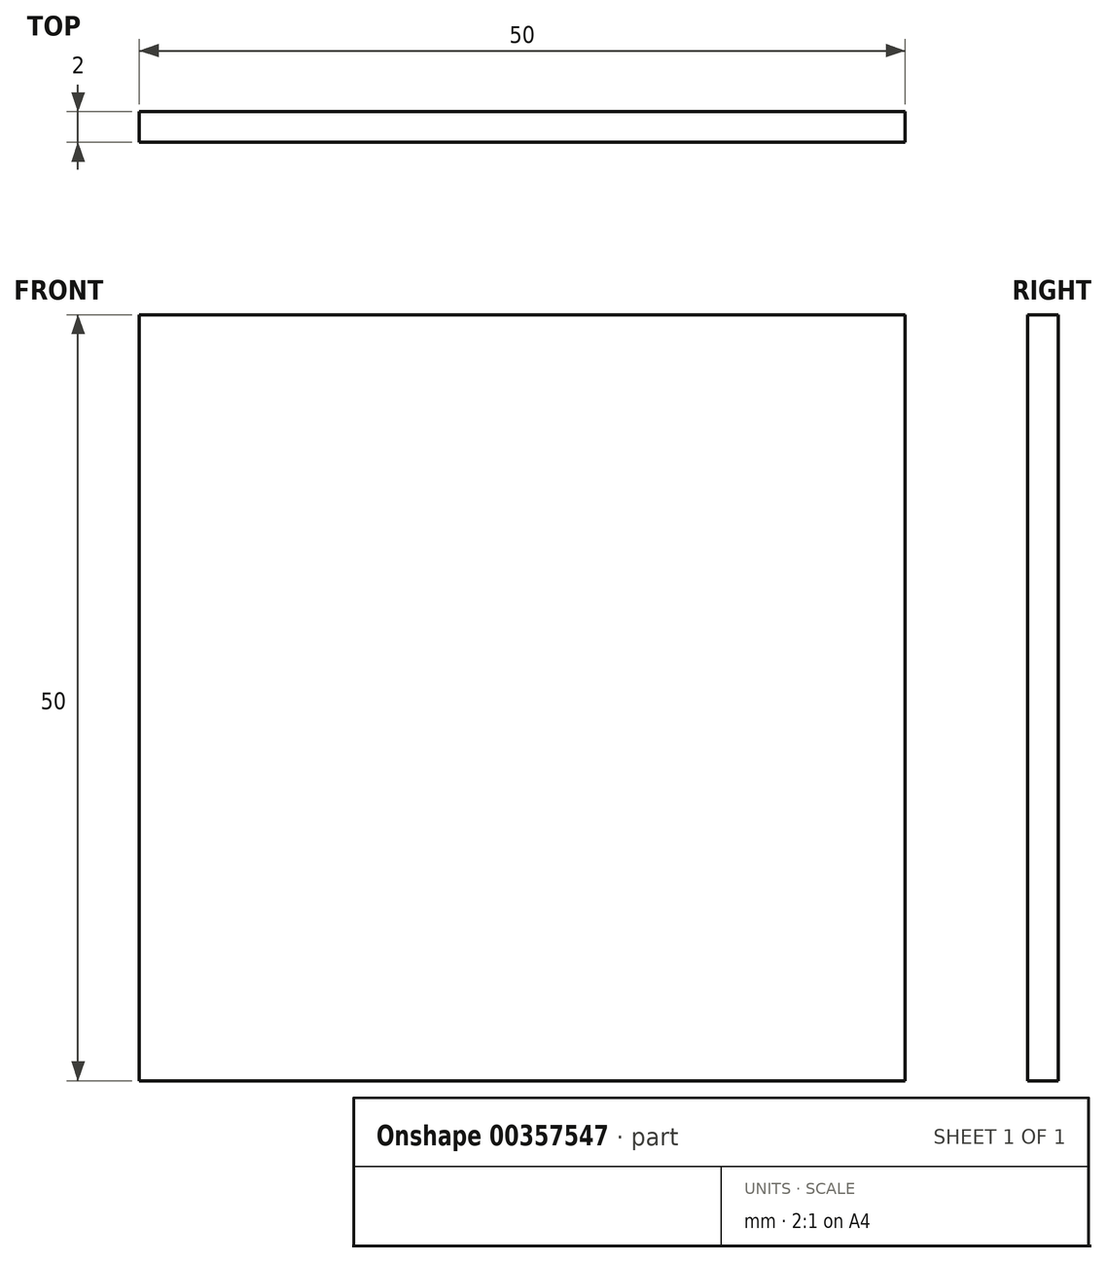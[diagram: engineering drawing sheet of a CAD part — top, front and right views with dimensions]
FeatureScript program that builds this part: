
annotation { "Feature Type Name" : "Feature", "Feature Type Description" : "" }
export const myFeature = defineFeature(function(context is Context, id is Id, definition is map)
    precondition{}
    {
        {
            var Q0;
            Q0=qCreatedBy(makeId("Front.planeOp"),FACE);
            var sketch = newSketch(context, id + "F0", { "sketchPlane" : qUnion([Q0])});
            skLineSegment(sketch, "E0.bottom", {"start": v(0, 0) * mm, "end": v(-50, 0) * mm});
            skLineSegment(sketch, "E0.top", {"start": v(0, 50) * mm, "end": v(-50, 50) * mm});
            skLineSegment(sketch, "E0.left", {"start": v(0, 0) * mm, "end": v(0, 50) * mm});
            skLineSegment(sketch, "E0.right", {"start": v(-50, 0) * mm, "end": v(-50, 50) * mm});
            skSolve(sketch);
        }
        {
            var Q0;
            Q0=makeQuery(id+"F0.imprint","IMPRINT",FACE,{"disambiguationData":[TD([[makeQuery(id+"F0.imprint","IMPRINT",EDGE,{"derivedFrom":sQuery(id+"F0.wireOp",EDGE,"E0.bottom")}),-1.0]])]});
            extrude(context, id + "F1", {"entities" : qUnion([Q0]), "depth" : 2 * mm});
        }
    });
